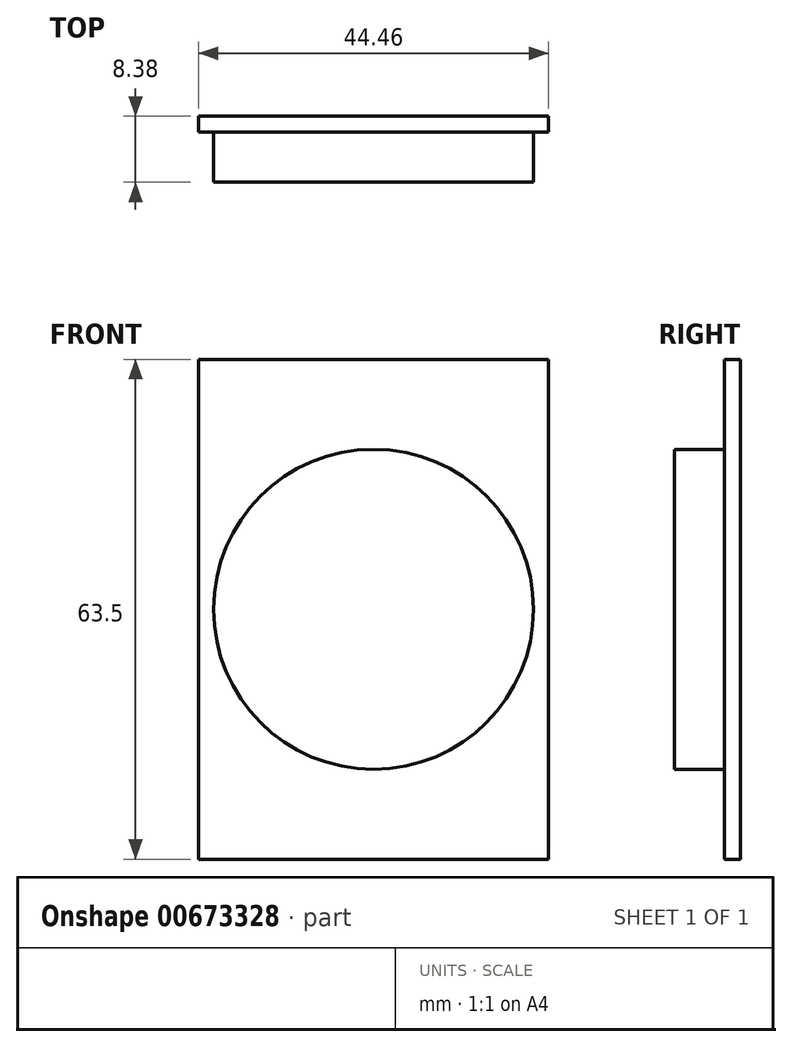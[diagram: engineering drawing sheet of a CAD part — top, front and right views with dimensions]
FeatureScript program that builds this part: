
annotation { "Feature Type Name" : "Feature", "Feature Type Description" : "" }
export const myFeature = defineFeature(function(context is Context, id is Id, definition is map)
    precondition{}
    {
        {
            var Q0;
            Q0=qCreatedBy(makeId("Front.planeOp"),FACE);
            var sketch = newSketch(context, id + "F0", { "sketchPlane" : qUnion([Q0])});
            skLineSegment(sketch, "E0.bottom", {"start": v(22.23, 31.75) * mm, "end": v(-22.23, 31.75) * mm});
            skLineSegment(sketch, "E0.top", {"start": v(22.23, -31.75) * mm, "end": v(-22.23, -31.75) * mm});
            skLineSegment(sketch, "E0.left", {"start": v(22.23, 31.75) * mm, "end": v(22.23, -31.75) * mm});
            skLineSegment(sketch, "E0.right", {"start": v(-22.23, 31.75) * mm, "end": v(-22.23, -31.75) * mm});
            skPoint(sketch, "E0.middle", {"position": v(0, 0) * mm});
            skSolve(sketch);
        }
        {
            var Q0;
            Q0 = qSketchRegion(id + "F0", true);
            extrude(context, id + "F1", {"entities" : qUnion([Q0]), "depth" : 2.03 * mm, "offsetDistance" : 25.4 * mm});
        }
        {
            var Q0;
            Q0=makeQuery(id+"F1.opExtrude","CAP_FACE",FACE,{"disambiguationData":[OSD([sQuery(id+"F0.wireOp",EDGE,"E0.bottom"),sQuery(id+"F0.wireOp",EDGE,"E0.top"),sQuery(id+"F0.wireOp",EDGE,"E0.left"),sQuery(id+"F0.wireOp",EDGE,"E0.right")])],"isStart":false});
            var sketch = newSketch(context, id + "F2", { "sketchPlane" : qUnion([Q0])});
            skCircle(sketch, "E1", {"center": v(0, 0) * mm, "radius": 20.32 * mm});
            skSolve(sketch);
        }
        {
            var Q0;
            Q0 = qSketchRegion(id + "F2", true);
            extrude(context, id + "F3", {"entities" : qUnion([Q0]), "operationType" : NewBodyOperationType.ADD, "depth" : 6.35 * mm, "offsetDistance" : 25.4 * mm});
        }
    });
